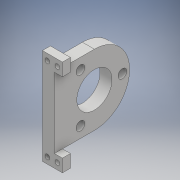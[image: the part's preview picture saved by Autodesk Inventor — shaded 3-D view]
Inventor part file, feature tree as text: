
AUTODESK INVENTOR PART (.ipt)
format: ipt  version: 2017 (Build 210142000, 142)  size: 180,224 bytes
history: native  units: mm
features: extrude x5, sketch x5
ambient origin geometry x8: Origin, YZ Plane, XZ Plane, XY Plane, X Axis, Y Axis, Z Axis, Center Point
bodies: Solid1 (feature_tree)
feature tree (10):
  extrude  "Extrusion1"  Depth=44.0mm
  extrude  "Extrusion2"  Depth=5.5mm
  extrude  "Extrusion3"  Depth=7.5mm TaperAngle=0.0deg
  extrude  "Extrusion5"  Depth=5.5mm
  extrude  "Extrusion7"  Depth=10.0mm TaperAngle=0.0deg
  sketch  "Sketch1"  dims[d0=22.0mm d1=44.0mm]
  sketch  "Sketch2"  dims[d2=35.0mm d3=5.5mm]
  sketch  "Sketch3"  dims[d4=30.0mm d6=360.0deg d8=7.5mm d9=0.0mm]
  sketch  "Sketch5"  dims[d10=35.0mm d11=5.5mm]
  sketch  "Sketch8"  dims[d12=30.0mm d14=360.0deg d16=10.0mm d17=0.0mm d18=25.0mm d19=90.0deg d20=50.0mm d21=25.0mm d22=5.0mm d23=30.0mm d24=5.0mm d25=60.0mm d26=5.0mm d27=7.5mm d28=0.0mm d41=5.0mm d42=12.5mm d43=0.0mm d44=0.0mm d55=5.0mm d56=0.0mm]
